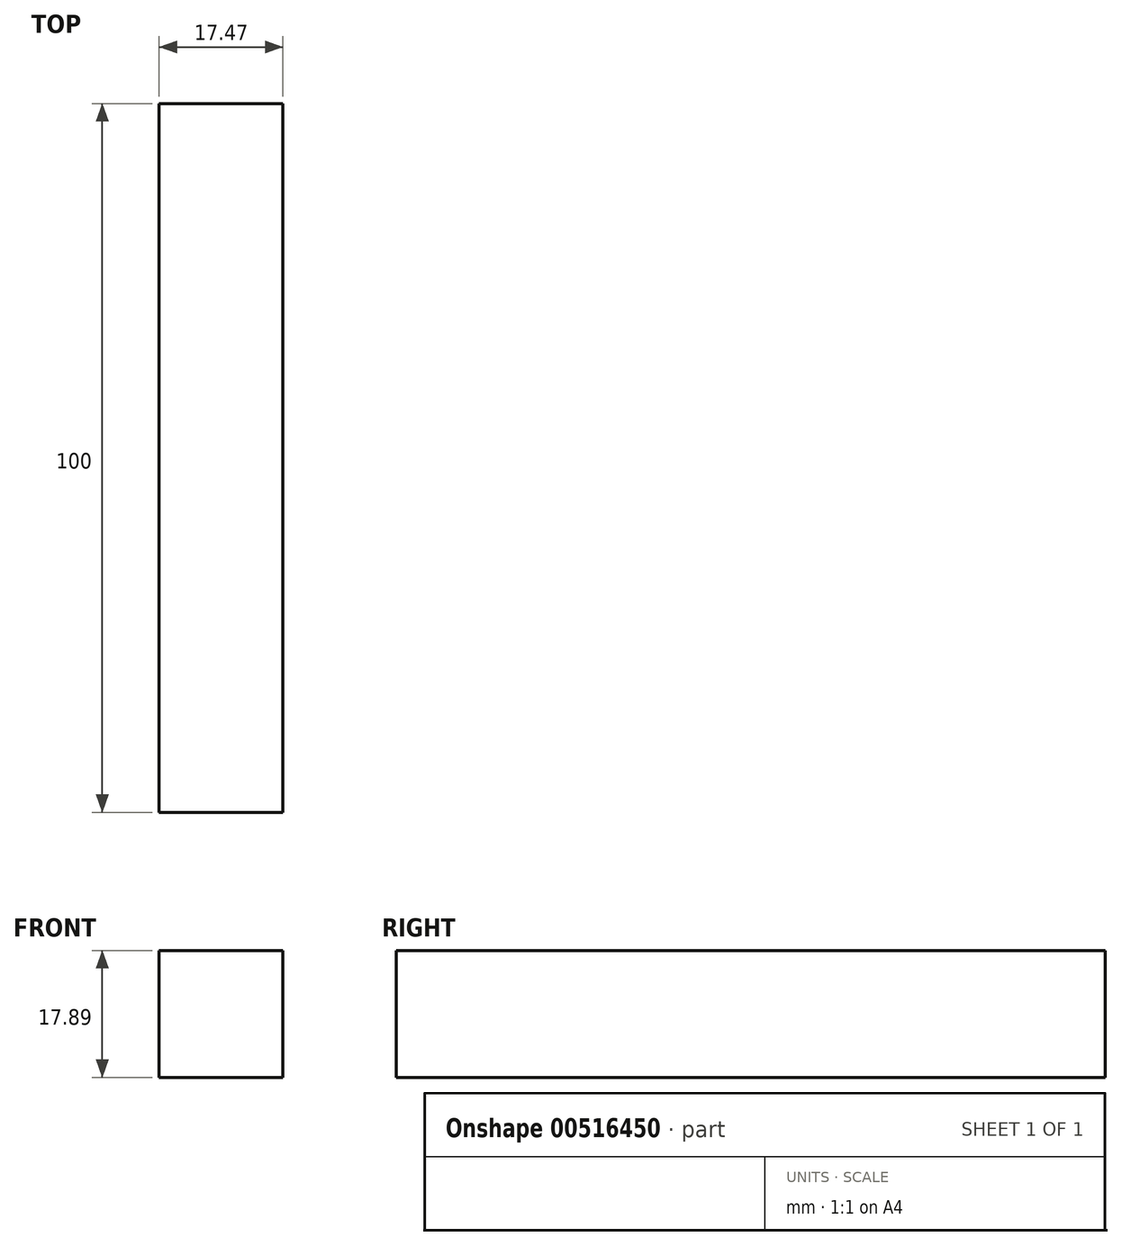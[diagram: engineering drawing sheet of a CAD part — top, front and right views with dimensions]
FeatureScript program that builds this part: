
annotation { "Feature Type Name" : "Feature", "Feature Type Description" : "" }
export const myFeature = defineFeature(function(context is Context, id is Id, definition is map)
    precondition{}
    {
        {
            var Q0;
            Q0=qCreatedBy(makeId("Front.planeOp"),FACE);
            var sketch = newSketch(context, id + "F0", { "sketchPlane" : qUnion([Q0])});
            skLineSegment(sketch, "E0.bottom", {"start": v(-68.29, 32) * mm, "end": v(-50.82, 32) * mm});
            skLineSegment(sketch, "E0.top", {"start": v(-68.29, 49.88) * mm, "end": v(-50.82, 49.88) * mm});
            skLineSegment(sketch, "E0.left", {"start": v(-68.29, 32) * mm, "end": v(-68.29, 49.88) * mm});
            skLineSegment(sketch, "E0.right", {"start": v(-50.82, 32) * mm, "end": v(-50.82, 49.88) * mm});
            skSolve(sketch);
        }
        {
            var Q0;
            Q0=qSketchRegion(id+"F0",true);
            extrude(context, id + "F1", {"entities" : qUnion([Q0]), "depth" : 100 * mm, "offsetDistance" : 25 * mm});
        }
    });
